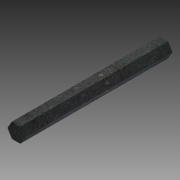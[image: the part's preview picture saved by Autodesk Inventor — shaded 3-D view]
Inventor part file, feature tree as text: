
AUTODESK INVENTOR PART (.ipt)
format: ipt  version: 2014 SP1 (Build 180222100, 222)  size: 81,920 bytes
history: native  units: in
note: dims shown in document units (in); Inventor stores cm internally (conversion verified against a paired STEP export)
features: extrude x1, sketch x1
ambient origin geometry x8: Origin, YZ Plane, XZ Plane, XY Plane, X Axis, Y Axis, Z Axis, Center Point
bodies: Solid1 (feature_tree)
feature tree (2):
  extrude  "Extrusion1"  Depth=5.0in TaperAngle=0.0deg
  sketch  "Sketch1"  dims[d0=0.5in d1=5.0in d2=0.0in]
